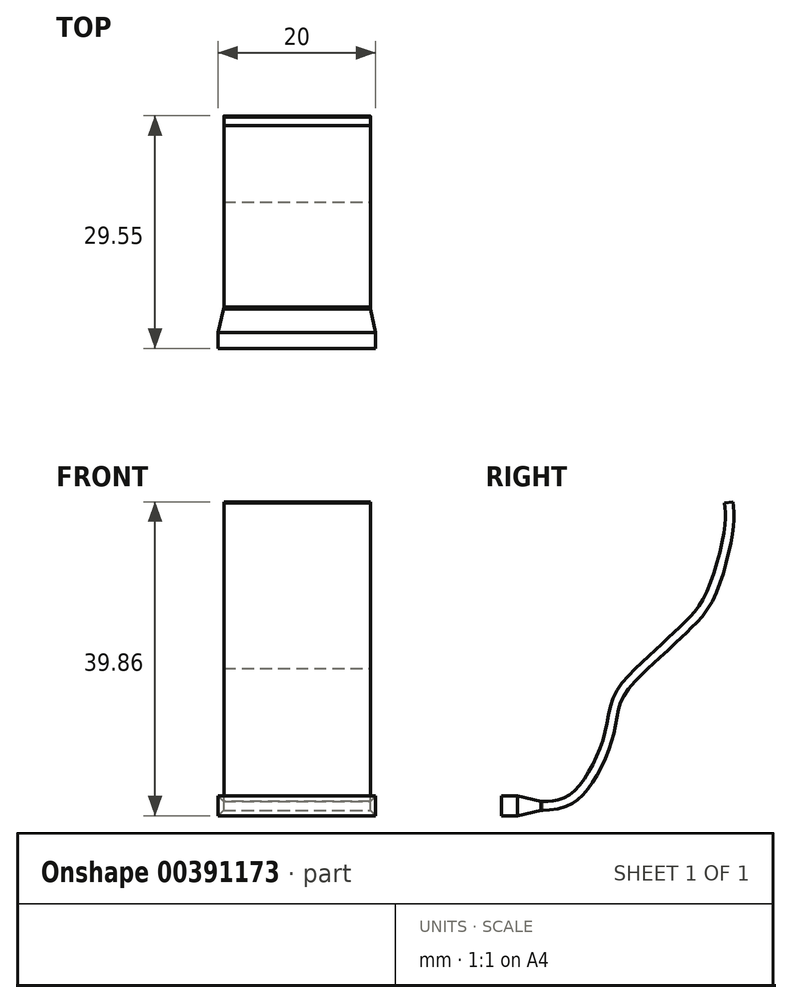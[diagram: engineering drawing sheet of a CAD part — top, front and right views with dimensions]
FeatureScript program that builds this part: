
annotation { "Feature Type Name" : "Feature", "Feature Type Description" : "" }
export const myFeature = defineFeature(function(context is Context, id is Id, definition is map)
    precondition{}
    {
        {
            var Q0;
            Q0=qCreatedBy(makeId("Front.planeOp"),FACE);
            var sketch = newSketch(context, id + "F0", { "sketchPlane" : qUnion([Q0])});
            skLineSegment(sketch, "E0.bottom", {"start": v(10, 1.25) * mm, "end": v(-10, 1.25) * mm});
            skLineSegment(sketch, "E0.top", {"start": v(10, -1.25) * mm, "end": v(-10, -1.25) * mm});
            skLineSegment(sketch, "E0.left", {"start": v(10, 1.25) * mm, "end": v(10, -1.25) * mm});
            skLineSegment(sketch, "E0.right", {"start": v(-10, 1.25) * mm, "end": v(-10, -1.25) * mm});
            skPoint(sketch, "E0.middle", {"position": v(0, 0) * mm});
            skSolve(sketch);
        }
        {
            var Q0;
            Q0=makeQuery(id+"F0.imprint","IMPRINT",FACE,{"disambiguationData":[TD([[makeQuery(id+"F0.imprint","IMPRINT",EDGE,{"derivedFrom":sQuery(id+"F0.wireOp",EDGE,"E0.bottom")}),1.0]])]});
            extrude(context, id + "F1", {"entities" : qUnion([Q0]), "depth" : 2 * mm});
        }
        {
            var Q0;
            Q0=makeQuery(id+"F1.opExtrude","CAP_FACE",FACE,{"disambiguationData":[OSD([sQuery(id+"F0.wireOp",EDGE,"E0.bottom"),sQuery(id+"F0.wireOp",EDGE,"E0.top"),sQuery(id+"F0.wireOp",EDGE,"E0.left"),sQuery(id+"F0.wireOp",EDGE,"E0.right")])],"isStart":true});
            extrude(context, id + "F2", {"entities" : qUnion([Q0]), "operationType" : NewBodyOperationType.ADD, "depth" : 3 * mm, "hasDraft" : true, "draftAngle" : 12.5 * degree, "draftPullDirection" : true});
        }
        {
            var Q0;
            Q0=makeQuery(id+"F2.opExtrude","CAP_EDGE",EDGE,{"disambiguationData":[OSD([sQuery(id+"F0.wireOp",EDGE,"E0.left")])],"isStart":false});
            cPlane(context, id + "F3", {"entities" : qUnion([Q0]), "cplaneType" : CPlaneType.LINE_ANGLE, "offset" : 25 * mm, "angle" : 0 * degree, "width" : 150 * mm, "height" : 150 * mm});
        }
        {
            var Q0;
            Q0=qCreatedBy(id+"F3.planeOp",FACE);
            var sketch = newSketch(context, id + "F4", { "sketchPlane" : qUnion([Q0])});
            skLineSegment(sketch, "E1", {"start": v(0, 0) * mm, "end": v(3, 0) * mm});
            skLineSegment(sketch, "E2", {"start": v(3, 0) * mm, "end": v(3.25, 0) * mm});
            skLineSegment(sketch, "E3", {"start": v(3.25, 0) * mm, "end": v(3.25, 0.55) * mm});
            skLineSegment(sketch, "E4", {"start": v(3.25, 0) * mm, "end": v(3.25, -0.55) * mm});
            skFitSpline(sketch, "E5", {"points": [v(3.25, 0.55) * mm, v(4.89, 0.71) * mm, v(7.05, 1.7) * mm, v(9.38, 4.87) * mm, v(11.15, 9.34) * mm, v(12.3, 13.98) * mm, v(15.86, 18.23) * mm], "startDerivative": vector(14.29, 0.61) * mm, "endDerivative": vector(20.78, 19.8) * mm});
            skFitSpline(sketch, "E6.0", {"points": [v(3.3, -0.55) * mm, v(3.6, -0.54) * mm, v(4.23, -0.5) * mm, v(5.16, -0.37) * mm, v(5.97, -0.14) * mm, v(6.6, 0.11) * mm, v(7.13, 0.4) * mm, v(7.54, 0.68) * mm, v(7.95, 1) * mm, v(8.41, 1.46) * mm, v(8.92, 2.06) * mm, v(9.39, 2.71) * mm, v(9.82, 3.4) * mm, v(10.23, 4.1) * mm, v(10.74, 5.07) * mm, v(11.21, 6.08) * mm, v(11.63, 7.12) * mm, v(11.9, 7.92) * mm, v(12.15, 8.74) * mm, v(12.34, 9.58) * mm, v(12.49, 10.39) * mm, v(12.62, 11.17) * mm, v(12.77, 11.9) * mm, v(12.94, 12.6) * mm, v(13.16, 13.23) * mm, v(13.44, 13.82) * mm, v(13.81, 14.41) * mm, v(14.41, 15.2) * mm, v(15.34, 16.2) * mm, v(16.19, 17.02) * mm, v(16.62, 17.43) * mm]});
            skLineSegment(sketch, "E7", {"start": v(3.25, -0.55) * mm, "end": v(3.3, -0.55) * mm});
            skFitSpline(sketch, "E8", {"points": [v(15.86, 18.23) * mm, v(20.88, 22.96) * mm, v(23.97, 26.92) * mm, v(26.36, 35.68) * mm, v(26.32, 38.48) * mm], "startDerivative": vector(19.5, 18.28) * mm, "endDerivative": vector(-1.57, 13.02) * mm});
            skFitSpline(sketch, "E9.0", {"points": [v(16.61, 17.42) * mm, v(17.43, 18.19) * mm, v(18.65, 19.33) * mm, v(20.18, 20.77) * mm, v(21.08, 21.62) * mm, v(21.74, 22.26) * mm, v(22.39, 22.88) * mm, v(23.17, 23.68) * mm, v(24.05, 24.8) * mm, v(24.86, 26.16) * mm, v(25.59, 27.85) * mm, v(26.22, 29.75) * mm, v(26.76, 31.72) * mm, v(27.18, 33.62) * mm, v(27.4, 35.04) * mm, v(27.5, 36) * mm, v(27.55, 36.87) * mm, v(27.51, 37.76) * mm, v(27.44, 38.34) * mm, v(27.4, 38.61) * mm]});
            skLineSegment(sketch, "E10", {"start": v(26.32, 38.48) * mm, "end": v(27.4, 38.61) * mm});
            skSolve(sketch);
        }
        {
            var Q0;
            Q0=makeQuery(id+"F4.imprint","IMPRINT",FACE,{"disambiguationData":[TD([[makeQuery(id+"F4.imprint","IMPRINT",EDGE,{"derivedFrom":sQuery(id+"F4.wireOp",EDGE,"E3")}),-1.0]])]});
            extrude(context, id + "F5", {"entities" : qUnion([Q0]), "operationType" : NewBodyOperationType.ADD, "oppositeDirection" : true, "depth" : 18.6 * mm});
        }
        {
            var Q1;
            Q1=makeQuery(id+"F5.opExtrude","SWEPT_FACE",FACE,{"disambiguationData":[OSD([sQuery(id+"F4.wireOp",EDGE,"E3"),sQuery(id+"F4.wireOp",EDGE,"E4")])]});
            var Q2;
            Q2=makeQuery(id+"F2.opExtrude","CAP_FACE",FACE,{"disambiguationData":[OSD([sQuery(id+"F0.wireOp",EDGE,"E0.bottom"),sQuery(id+"F0.wireOp",EDGE,"E0.top"),sQuery(id+"F0.wireOp",EDGE,"E0.left"),sQuery(id+"F0.wireOp",EDGE,"E0.right")])],"isStart":false});
            loft(context, id + "F6", {"operationType" : NewBodyOperationType.ADD, "sheetProfilesArray" : [{ "sheetProfileEntities" : qUnion([Q1]) }, { "sheetProfileEntities" : qUnion([Q2]) }]});
        }
    });
